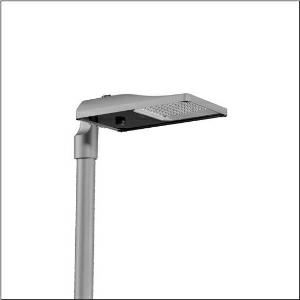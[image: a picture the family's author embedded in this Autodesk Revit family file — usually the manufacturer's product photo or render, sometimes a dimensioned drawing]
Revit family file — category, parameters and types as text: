
# Revit family: streetlight_sl_31_midi___st0_5a_5xh7b31t08qa_33e3
name_source: partatom
category: Lighting Fixtures
units: mm (PartAtom-declared; Revit-internal decimal feet)

## family parameters
Cut with Voids When Loaded = No
Host = Face
Light Source = No
Part Type = Normal
Room Calculation Point = No
Round Connector Dimension = Use Diameter
Shared = No

## types (1)
- --- (1 x LED, 24430 lm, 163.3 W, 3000K)
    Apparent Load = 163 VA
    CIE Flux Codes = 43 76 97 100 100
    Color Rendering = 70
    Color Temperature = 3000K
    Default Elevation = 1800 mm
    Description = Streetlight SL 31 midi D4i, Desk-Remote mast luminaire for post-top, side-entry; light control with lens of PMMA; light distribution: ST0.5a, direct asymmetric distribution, for standard-compliant lighting for roads and squares; LED: luminous flux: 24.430lm, light colour: 730, colour temperature: 3000K; luminous efficacy: 149,6lm/W; control: pre-setting: logarithmic dimming characteristic, flexible luminous flux parameterisation, time-dependent luminous flux control, constant luminous flux control, power reduction, intelligent temperature release in ECG and LED module, overheat protection; luminaire housing, of diecast aluminium, Siteco® metallic grey (DB 702S), corrosivity category C5 high according to DIN EN ISO 12944; cover of toughened safety glass, transparent, opened without tools; mast flange of diecast aluminium, Siteco® metallic grey (DB 702S), spigot size: 76/60mm, mast flange included unmounted; with cable H07RN-F 2x 1.5mm², cable length: 14,5m, connection cable pre-assembled; mains connection: 220..240V, AC, 50/60Hz; power consumption (at start of service life): 163,3W / (at end of service life): 178,2W / (with reduced operation 50%): 73W; protection rating (complete): IP66; insulation class (complete): insulation class II (safety insulation); impact resistance: IK09; certification: CE, ENEC, ENEC+, VDE, UKCA, ZD4i; permissible operating ambient temperature for outdoor applications: -40..+50°C; packaging unit: 1 piece

Light Distribution: ST0.5a
    Height = 79 mm
    Lamp = 1 x LED
    Lamp Light Flux = 24430 lm
    Lamp Power = 163.3 W
    Lamp count = 1
    Length = 577 mm
    Luminous efficacy = 150 lm/W
    Manufacturer = Siteco
    ModVariant = No
    Model = 5XH7B31T08QA
    Number of Poles = 1
    OnlyDefault = Yes
    Power Factor = 1
    Product Name = Streetlight SL 31 midi | ST0.5a
    Product group = mast luminaire | pylon top
    ProductGroupID = 6100
    Protection Class = Protection class II
    Protection Degree = IP 66
    RLX_Detail_Level = 1
    RLX_Emergency_Light_Flux = 0 lm
    RLX_Emergency_Type = 0
    RLX_Emergency_Type_DB = No
    RlxData = <blob elided: 54385 chars, md5=7193fa76>
    Socket = socket
    Standby Power = 0 W
    System Light Flux = 24430 lm
    System Power = 163 W
    Type Comments = factory setting: luminous flux: 100 % | dim-lin: 254 | 865 mA
    Type Image = l_1300321.jpg
    URL = http://relux.com
    VarID = @adj_077759
    Voltage = 0 V
    Weight = 0.00 kg
    Width = 362 mm

## geometry (parser evidence)
native form markers: Blend x4, Sweep x11
no freeform markers — native parametric forms only
